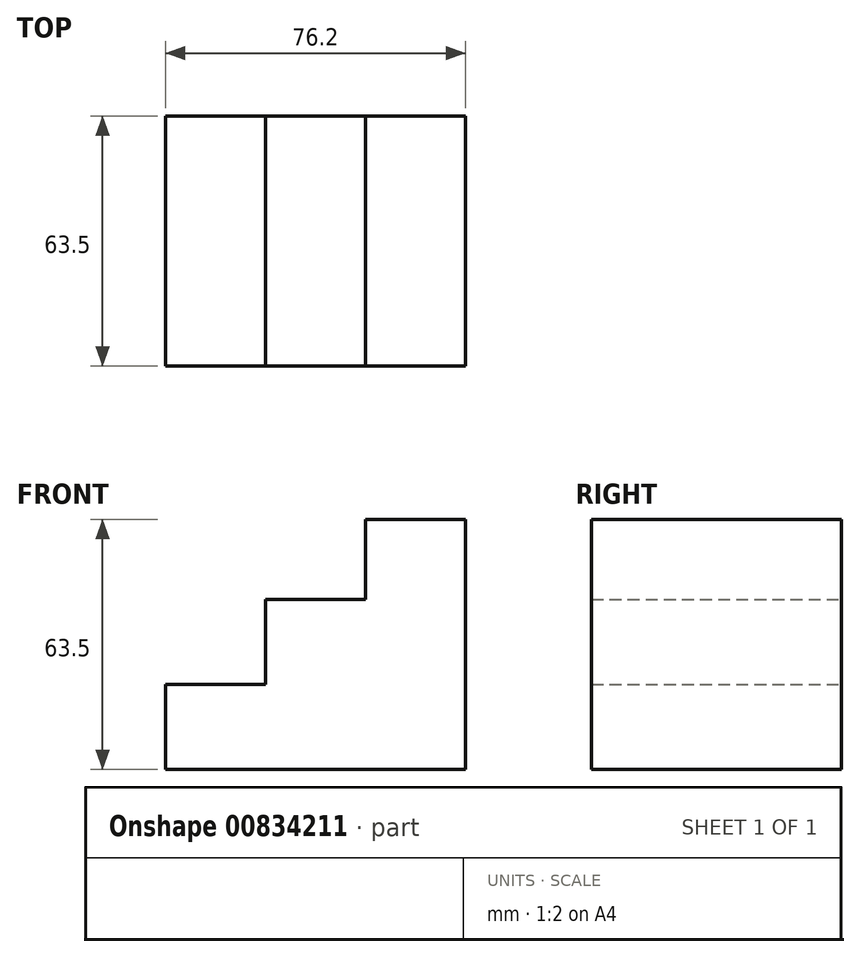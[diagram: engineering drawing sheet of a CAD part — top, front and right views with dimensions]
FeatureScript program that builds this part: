
annotation { "Feature Type Name" : "Feature", "Feature Type Description" : "" }
export const myFeature = defineFeature(function(context is Context, id is Id, definition is map)
    precondition{}
    {
        {
            var Q0;
            Q0=qCreatedBy(makeId("Front.planeOp"),FACE);
            var sketch = newSketch(context, id + "F0", { "sketchPlane" : qUnion([Q0])});
            skLineSegment(sketch, "E0", {"start": v(0, 0) * mm, "end": v(0, -63.5) * mm});
            skLineSegment(sketch, "E1", {"start": v(0, 0) * mm, "end": v(-25.4, 0) * mm});
            skLineSegment(sketch, "E2", {"start": v(-25.4, 0) * mm, "end": v(-25.4, -20.32) * mm});
            skLineSegment(sketch, "E3", {"start": v(-25.4, -20.32) * mm, "end": v(-50.8, -20.32) * mm});
            skLineSegment(sketch, "E4", {"start": v(-50.8, -20.32) * mm, "end": v(-50.8, -41.91) * mm});
            skLineSegment(sketch, "E5", {"start": v(-50.8, -41.91) * mm, "end": v(-76.2, -41.91) * mm});
            skLineSegment(sketch, "E6", {"start": v(-76.2, -41.91) * mm, "end": v(-76.2, -63.5) * mm});
            skLineSegment(sketch, "E7", {"start": v(-76.2, -63.5) * mm, "end": v(0, -63.5) * mm});
            skSolve(sketch);
        }
        {
            var Q0;
            Q0=makeQuery(id+"F0.imprint","IMPRINT",FACE,{"disambiguationData":[TD([[makeQuery(id+"F0.imprint","IMPRINT",EDGE,{"derivedFrom":sQuery(id+"F0.wireOp",EDGE,"E0")}),-1.0]])]});
            extrude(context, id + "F1", {"entities" : qUnion([Q0]), "depth" : 63.5 * mm, "offsetDistance" : 25.4 * mm});
        }
    });
